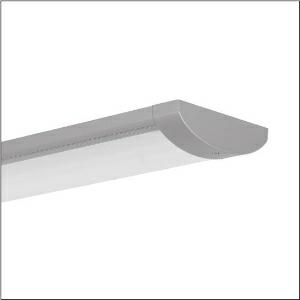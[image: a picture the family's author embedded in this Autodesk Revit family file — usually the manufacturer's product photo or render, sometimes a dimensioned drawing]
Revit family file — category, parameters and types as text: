
# Revit family: tv_20_5xa86174n0x
name_source: partatom
category: Lighting Fixtures
units: mm (PartAtom-declared; Revit-internal decimal feet)

## family parameters
Cut with Voids When Loaded = No
Host = Face
Light Source = No
Part Type = Normal
Room Calculation Point = No
Round Connector Dimension = Use Diameter
Shared = No

## types (1)
- TV 20 (1 x LED 4000K / CRI = 80 (unbekannt), 5120 lm, 4000K)
    Apparent Load = 50 VA
    CIE Flux Codes = 48 78 95 99 100
    Color Rendering = 80
    Color Temperature = 4000K
    Default Elevation = 1800 mm
    Description = TV 20, vandal-proof luminaire, primary light control with specular reflector, of aluminium, matt, primary optical cover: enclosure, of PC, frosted, light emission: direct distribution, primary light characteristic: symmetric, installation type: surface-mounted, LED rated luminous flux: 5.120 lm, light colour: 840, colour temperature: 4000K, control gear: ECG, mains connection: 230V, AC, 50Hz, rated input power: 50W, luminaire housing, of aluminium, coated, Siteco® metallic grey (DB 702S), length: 1.561 mm, width: 260 mm, height: 70mm, protection rating (complete): IP65, insulation class (complete): insulation class I (protective earthing), certification: CE, protection symbol: F, impact resistance: 2x IK10, standard: EN 60598, packaging unit: 1 piece
    Height = 70 mm
    Lamp = 1 x LED 4000K / CRI >= 80 (unbekannt)
    Lamp Light Flux = 5120 lm
    Lamp count = 1
    Length = 1561 mm
    Luminous efficacy = 102 lm/W
    Manufacturer = Siteco
    ModVariant = No
    Model = 5XA86174N0X
    Mounting Place = Ceiling
    Mounting Type = Surface mounted
    Number of Poles = 1
    OnlyDefault = Yes
    Power Factor = 1
    Product Name = TV 20
    Product group = vandal-proof luminaire
    ProductGroupID = 307
    Protection Class = Protection class I
    Protection Degree = IP 65
    RLX_Detail_Level = 1
    RlxData = <blob elided: 25209 chars, md5=0d4cd324>
    Socket = socket
    Standby Power = 0 W
    System Light Flux = 5120 lm
    System Power = 50 W
    Type Comments = Product without accessories
    Type Image = l_1004809.jpg
    URL = http://relux.com
    VarID = ---
    Voltage = 0 V
    Weight = 0.00 kg
    Width = 260 mm

## geometry (parser evidence)
native form markers: Blend x4, Sweep x11
no freeform markers — native parametric forms only
